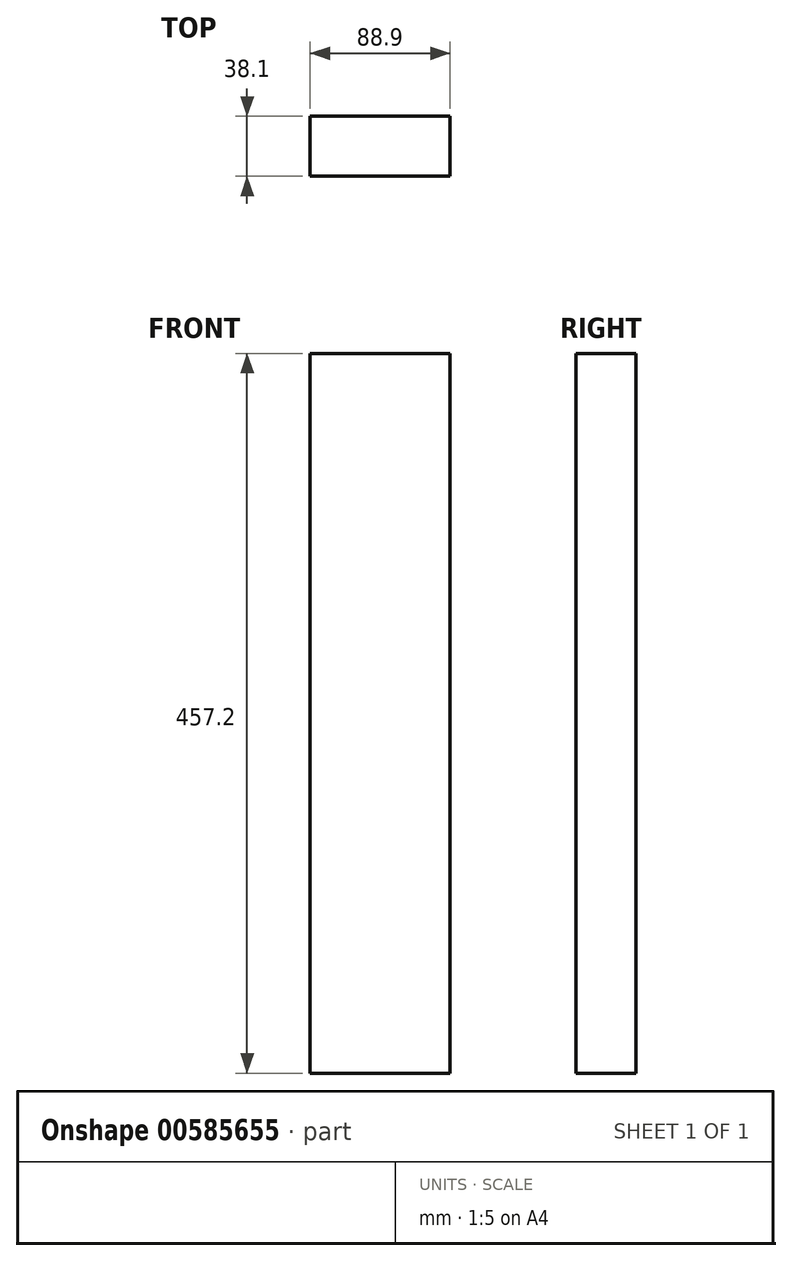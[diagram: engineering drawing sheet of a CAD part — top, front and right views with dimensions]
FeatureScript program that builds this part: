
annotation { "Feature Type Name" : "Feature", "Feature Type Description" : "" }
export const myFeature = defineFeature(function(context is Context, id is Id, definition is map)
    precondition{}
    {
        {
            var Q0;
            Q0=qCreatedBy(makeId("Front.planeOp"),FACE);
            var sketch = newSketch(context, id + "F0", { "sketchPlane" : qUnion([Q0])});
            skLineSegment(sketch, "E0", {"start": v(0, 0) * mm, "end": v(88.9, 0) * mm});
            skLineSegment(sketch, "E1", {"start": v(88.9, 0) * mm, "end": v(88.9, 457.2) * mm});
            skLineSegment(sketch, "E2", {"start": v(0, 457.2) * mm, "end": v(0, 0) * mm});
            skLineSegment(sketch, "E3", {"start": v(0, 457.2) * mm, "end": v(88.9, 457.2) * mm});
            skPoint(sketch, "E4.orphan", {"position": v(0, 484.77) * mm});
            skSolve(sketch);
        }
        {
            var Q0;
            Q0=makeQuery(id+"F0.imprint","IMPRINT",FACE,{"disambiguationData":[TD([[makeQuery(id+"F0.imprint","IMPRINT",EDGE,{"derivedFrom":sQuery(id+"F0.wireOp",EDGE,"E0")}),1.0]])]});
            var Q1;
            Q1=qConstructionFilter(qBodyType(qCreatedBy(id+"F0",EDGE),BodyType.WIRE),ConstructionObject.NO);
            extrude(context, id + "F1", {"entities" : qUnion([Q0]), "surfaceEntities" : qUnion([Q1]), "oppositeDirection" : true, "depth" : 38.1 * mm, "offsetDistance" : 25.4 * mm});
        }
    });
